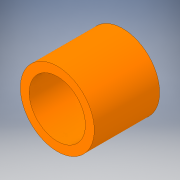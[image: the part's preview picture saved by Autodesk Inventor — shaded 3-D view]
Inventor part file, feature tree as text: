
AUTODESK INVENTOR PART (.ipt)
format: ipt  version: 2018 (Build 220112000, 112)  size: 112,640 bytes
history: native  units: in
note: dims shown in document units (in); Inventor stores cm internally (conversion verified against a paired STEP export)
features: extrude x1, sketch x1
ambient origin geometry x8: Origin, YZ Plane, XZ Plane, XY Plane, X Axis, Y Axis, Z Axis, Center Point
bodies: Solid1 (feature_tree)
feature tree (2):
  extrude  "Extrusion1"  Depth=1.163in
  sketch  "Sketch1"  dims[d0=1.315in d1=1.0in d2=1.163in d3=0.0in]
